# Revit family: rs_pro_connect_5100_led_058708
name_source: partatom
category: Leuchten
revit_build: Autodesk Revit 2016 (Build: 20190508_0715(x64)
units: mm (PartAtom-declared; Revit-internal decimal feet)

## family parameters
Basisbauteil = Fläche
Beim Laden mit Abzugskörper schneiden = Nein
Bemaßung runder Anschluss = Durchmesser verwenden
Gemeinsam genutzt = Nein
Lichtquelle = Nein
Raumberechnungspunkt = Nein
Teiletyp = Normal

## types (1)
- RS PRO Connect 5100 LED (1 x , 4206 lm, 4000 K)
    Beschreibung = Dimensions (L x W x H): 58 x 1370 x 87 mm; Mains power supply: 220 – 240 V / 50 – 60 Hz; Sensor Technology: High frequency; Transmitter power: < 1 mW; HF-system: 5,8 GHz; Output: 32 W; Interconnection: Yes; Luminous flux: 4206 lm; Luminous flux, emergency light: 687 lm; Colour temperature: 4000 K; Colour variation LED: SDCM3; Colour Rendering Index CRI: 80-89; With lamp: Yes, STEINEL LED system; Lamp: LED cannot be replaced; LED life expectancy (max. °C): 60000 h; Drop in luminous flux in accordance with LM80: L80B10; Base: without; LED cooling system: Passive Thermo Control; With motion detector: Yes; Detection: also through glass, wood and stud walls; Detection angle: 360 °; Angle of aperture: 160 °; Electronic scalability: Yes; Mechanical scalability: No; Reach, radial: Ø 10 m (79 m²); Reach, tangential: Ø 10 m (79 m²); Main light adjustable: 50 - 100 %; Continuous light: selectable; Photo-cell controller: Yes; Twilight setting: 2 – 2000 lx; Time setting: 5 sec – 60 min; Basic light level function: Yes; Basic light level function time: 10-30 min, all night; Functions: Group parameterisation, Manual ON / ON-OFF, Master/slave override, Neighbouring-group function, Presence function, Emergency light in compliance with EN 60598-2-22 for 3h; Soft light start: No; Impact resistance: IK07; IP-rating: IP66; Protection class: II; Ambient temperature: -20 – 40 °C; Housing material: Plastic; Cover material: Plastic, structured; Manufacturer's Warranty: 5 years; Settings via: Bluetooth; With remote control: Yes; Version: Emergency light; PU1, EAN: 4007841058708
    Color Rendering = 80-89
    Color Temperature = 4000 K
    Frequency = 60 Hz, 50 Hz
    Height = 87 mm
    Hersteller = Steinel
    Lamp Light Flux = 4206 lm
    Lamp count = 1
    Lampe = 1 x
    Length = 58 mm
    Luminous efficacy = 0 lm/W
    ModVariant = Nein
    Modell = 058708
    Mounting Type = Surface mounted
    Number of Poles = 1
    OnlyDefault = Ja
    Power Factor = 1
    Product Name = RS PRO Connect 5100 LED
    Product group = Sensor-switched indoor light
    ProductGroupID = 30
    Protection Class = Protection class II
    Protection Degree = Degree of protection
    RlxData = <blob elided: 18305 chars, md5=10b231ec>
    Scheinlast = 32 VA
    Socket = socket
    Standby Power = 0 W
    System Light Flux = 0 lm
    System Power = 32 W
    Typenbild = produkt1_058708.jpg
    Typenkommentare = Product without accessories
    URL = http://relux.com
    VarID = ---
    Voltage = 0 V
    Vorgabe-Ansicht = 1800 mm
    Weight = 0.00 kg
    Width = 1370 mm

## geometry (parser evidence)
native form markers: Blend x4, Sweep x10
no freeform markers — native parametric forms only
